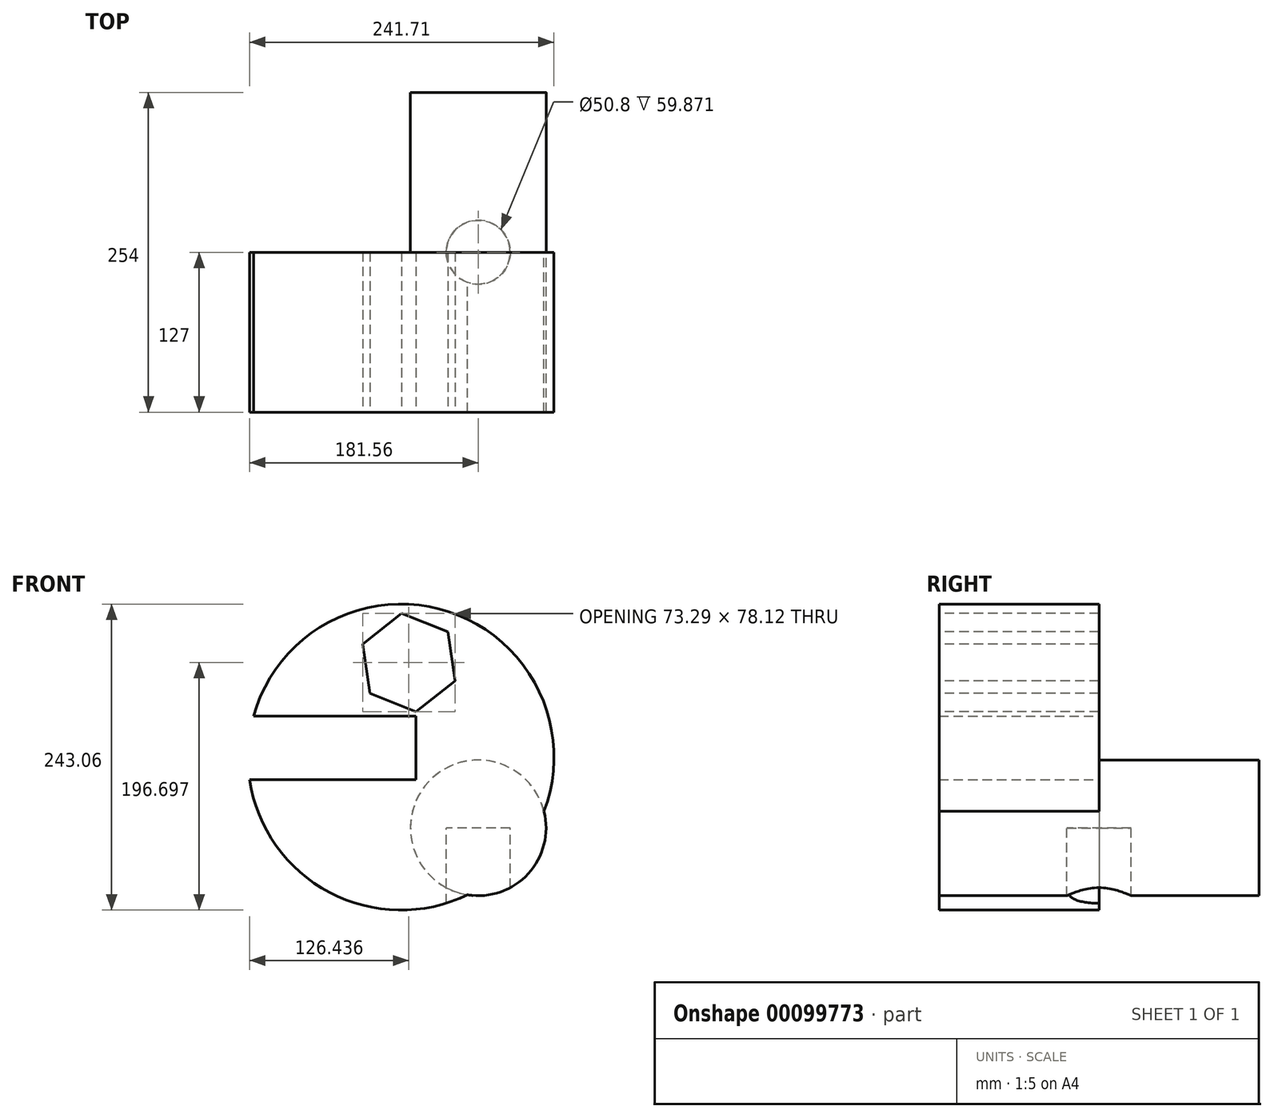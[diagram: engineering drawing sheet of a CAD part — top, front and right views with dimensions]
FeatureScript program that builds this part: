
annotation { "Feature Type Name" : "Feature", "Feature Type Description" : "" }
export const myFeature = defineFeature(function(context is Context, id is Id, definition is map)
    precondition{}
    {
        {
            var Q0;
            Q0=qCreatedBy(makeId("Front.planeOp"),FACE);
            var sketch = newSketch(context, id + "F0", { "sketchPlane" : qUnion([Q0])});
            skCircle(sketch, "E0", {"center": v(0, 0) * mm, "radius": 53.85 * mm});
            skSolve(sketch);
        }
        {
            var Q0;
            Q0=makeQuery(id+"F0.imprint","IMPRINT",FACE,{"disambiguationData":[TD([[makeQuery(id+"F0.imprint","IMPRINT",EDGE,{"derivedFrom":sQuery(id+"F0.wireOp",EDGE,"E0")}),1.0]])]});
            extrude(context, id + "F1", {"entities" : qUnion([Q0]), "endBound" : BoundingType.SYMMETRIC, "depth" : 254 * mm});
        }
        {
            var Q0;
            Q0=qCreatedBy(makeId("Front.planeOp"),FACE);
            var sketch = newSketch(context, id + "F2", { "sketchPlane" : qUnion([Q0])});
            skCircle(sketch, "E1", {"center": v(-61.37, 56.21) * mm, "radius": 121.53 * mm});
            skSolve(sketch);
        }
        {
            var Q0;
            Q0=makeQuery(id+"F2.imprint","IMPRINT",FACE,{"disambiguationData":[TD([[makeQuery(id+"F2.imprint","IMPRINT",EDGE,{"derivedFrom":sQuery(id+"F2.wireOp",EDGE,"E1")}),1.0]])]});
            extrude(context, id + "F3", {"entities" : qUnion([Q0]), "operationType" : NewBodyOperationType.ADD, "depth" : 127 * mm});
        }
        {
            var Q0;
            Q0=qCreatedBy(makeId("Top.planeOp"),FACE);
            var sketch = newSketch(context, id + "F4", { "sketchPlane" : qUnion([Q0])});
            skFitSpline(sketch, "E2", {"points": [v(0, 0) * mm, v(76.8, 49.6) * mm, v(77.56, 85.77) * mm, v(56.01, 143.5) * mm, v(33.7, 154.27) * mm, v(-38.66, 165.82) * mm, v(-84.07, 149.65) * mm, v(-125.64, 115.02) * mm, v(-136.41, 92.7) * mm, v(-140.26, 63.45) * mm, v(-139.5, 46.51) * mm, v(-129.49, -24.3) * mm, v(-122.56, -65.1) * mm, v(-114.1, -94.34) * mm, v(-108.7, -105.12) * mm, v(-81, -149) * mm, v(-68.68, -162.08) * mm, v(-55.6, -173.62) * mm, v(-30.96, -185.94) * mm, v(-8.64, -185.17) * mm, v(12.14, -183.63) * mm, v(73.71, -176.7) * mm, v(95.27, -153.6) * mm, v(104.5, -123.6) * mm, v(111.43, -87.41) * mm, v(107.58, -58.17) * mm, v(107.58, -14.3) * mm, v(103.73, 13.42) * mm, v(92.96, 82.69) * mm, v(87.57, 98.08) * mm, v(48.31, 171.97) * mm, v(9.06, 183.52) * mm, v(-91.77, 201.22) * mm, v(-160.27, 185.83) * mm, v(-228, 158.12) * mm, v(-264.18, 106.55) * mm, v(-288.81, 49.6) * mm, v(-301.13, 22.65) * mm, v(-288.81, -47.4) * mm, v(-280.35, -89.72) * mm, v(-266.5, -122.05) * mm, v(-245.7, -155.15) * mm, v(-221.08, -182.09) * mm, v(-200.3, -202.1) * mm, v(-149.5, -238.28) * mm, v(-134.87, -243.66) * mm, v(-54.82, -251.36) * mm, v(-34.04, -250.6) * mm, v(15.99, -244.43) * mm, v(39.08, -241.35) * mm, v(60.63, -238.28) * mm, v(73.71, -229.8) * mm, v(93.73, -215.18) * mm, v(102.96, -192.86) * mm, v(123.75, -149) * mm, v(129.13, -122.82) * mm, v(136.83, -59.7) * mm, v(129.13, -15.06) * mm, v(119.13, 34.2) * mm, v(107.58, 65.76) * mm, v(173.15, 309.43) * mm, v(29.07, 221.23) * mm, v(-54.05, 242.79) * mm, v(-160.27, 226.62) * mm, v(-291.9, 207.38) * mm, v(-400.42, 155.8) * mm, v(-587.23, 297.5) * mm, v(-486.62, 48.05) * mm, v(-487.4, -19.68) * mm, v(-478.93, -68.17) * mm, v(-449.68, -131.29) * mm, v(-435.82, -153.6) * mm, v(-401.96, -184.4) * mm, v(-376.56, -202.87) * mm, v(-271.82, -464.56) * mm, v(-273.42, -236.74) * mm, v(-232.62, -247.51) * mm, v(-208, -249.82) * mm, v(-189.52, -251.36) * mm], "startDerivative": vector(5395.72, 2678.82) * mm, "endDerivative": vector(2219.13, -211.56) * mm});
            skSolve(sketch);
        }
        {
            var Q0;
            Q0=makeQuery(id+"F1.opExtrude","CAP_FACE",FACE,{"disambiguationData":[OSD([sQuery(id+"F0.wireOp",EDGE,"E0")])],"isStart":false});
            var sketch = newSketch(context, id + "F5", { "sketchPlane" : qUnion([Q0])});
            skCircle(sketch, "E3.cCircle", {"center": v(-55.12, 131.38) * mm, "radius": 34.18 * mm, "construction": true});
            skLineSegment(sketch, "E3.0", {"start": v(-18.48, 116.73) * mm, "end": v(-49.48, 92.32) * mm});
            skLineSegment(sketch, "E3.1", {"start": v(-49.48, 92.32) * mm, "end": v(-86.13, 106.96) * mm});
            skLineSegment(sketch, "E3.2", {"start": v(-86.13, 106.96) * mm, "end": v(-91.77, 146.02) * mm});
            skLineSegment(sketch, "E3.3", {"start": v(-91.77, 146.02) * mm, "end": v(-60.76, 170.44) * mm});
            skLineSegment(sketch, "E3.4", {"start": v(-60.76, 170.44) * mm, "end": v(-24.12, 155.8) * mm});
            skLineSegment(sketch, "E3.5", {"start": v(-24.12, 155.8) * mm, "end": v(-18.48, 116.73) * mm});
            skPoint(sketch, "E3.0.midPoint", {"position": v(-33.98, 104.52) * mm});
            skSolve(sketch);
        }
        {
            var Q0;
            Q0=makeQuery(id+"F5.imprint","IMPRINT",FACE,{"disambiguationData":[TD([[makeQuery(id+"F5.imprint","IMPRINT",EDGE,{"derivedFrom":sQuery(id+"F5.wireOp",EDGE,"E3.0")}),-1.0]])]});
            extrude(context, id + "F6", {"entities" : qUnion([Q0]), "operationType" : NewBodyOperationType.REMOVE, "oppositeDirection" : true, "depth" : 281.2 * mm});
        }
        {
            var Q0;
            Q0=sQuery(id+"F4.wireOp",VERTEX,"E2.0.internal");
            var Q1;
            Q1=makeQuery(id+"F1.opExtrude","SWEPT_BODY",BODY,{"disambiguationData":[OSD([sQuery(id+"F0.wireOp",EDGE,"E0")])]});
            hole(context, id + "F7", {"style" : HoleStyle.SIMPLE, "endStyle" : HoleEndStyle.THROUGH, "holeDiameter" : 50.8 * mm, "locations" : qUnion([Q0]), "scope" : qUnion([Q1]), "isTappedThrough" : true});
        }
        {
            var Q0;
            Q0=makeQuery(id+"F3.boolean.opBoolean","MERGE",FACE,{"derivedFrom":[makeQuery(id+"F1.opExtrude","CAP_FACE",FACE,{"disambiguationData":[OSD([sQuery(id+"F0.wireOp",EDGE,"E0")])],"isStart":false}),makeQuery(id+"F3.opExtrude","CAP_FACE",FACE,{"disambiguationData":[OSD([sQuery(id+"F2.wireOp",EDGE,"E1")])],"isStart":false})]});
            var sketch = newSketch(context, id + "F8", { "sketchPlane" : qUnion([Q0])});
            skLineSegment(sketch, "E4.bottom", {"start": v(-49.48, 38.2) * mm, "end": v(-194.21, 38.2) * mm});
            skLineSegment(sketch, "E4.top", {"start": v(-49.48, 88.92) * mm, "end": v(-194.21, 88.92) * mm});
            skLineSegment(sketch, "E4.left", {"start": v(-49.48, 38.2) * mm, "end": v(-49.48, 88.92) * mm});
            skLineSegment(sketch, "E4.right", {"start": v(-194.21, 38.2) * mm, "end": v(-194.21, 88.92) * mm});
            skPoint(sketch, "E4.middle", {"position": v(-121.85, 63.56) * mm});
            skSolve(sketch);
        }
        {
            var Q0;
            Q0 = qSketchRegion(id + "F8", true);
            extrude(context, id + "F9", {"entities" : qUnion([Q0]), "operationType" : NewBodyOperationType.REMOVE, "oppositeDirection" : true, "depth" : 479.88 * mm});
        }
    });
